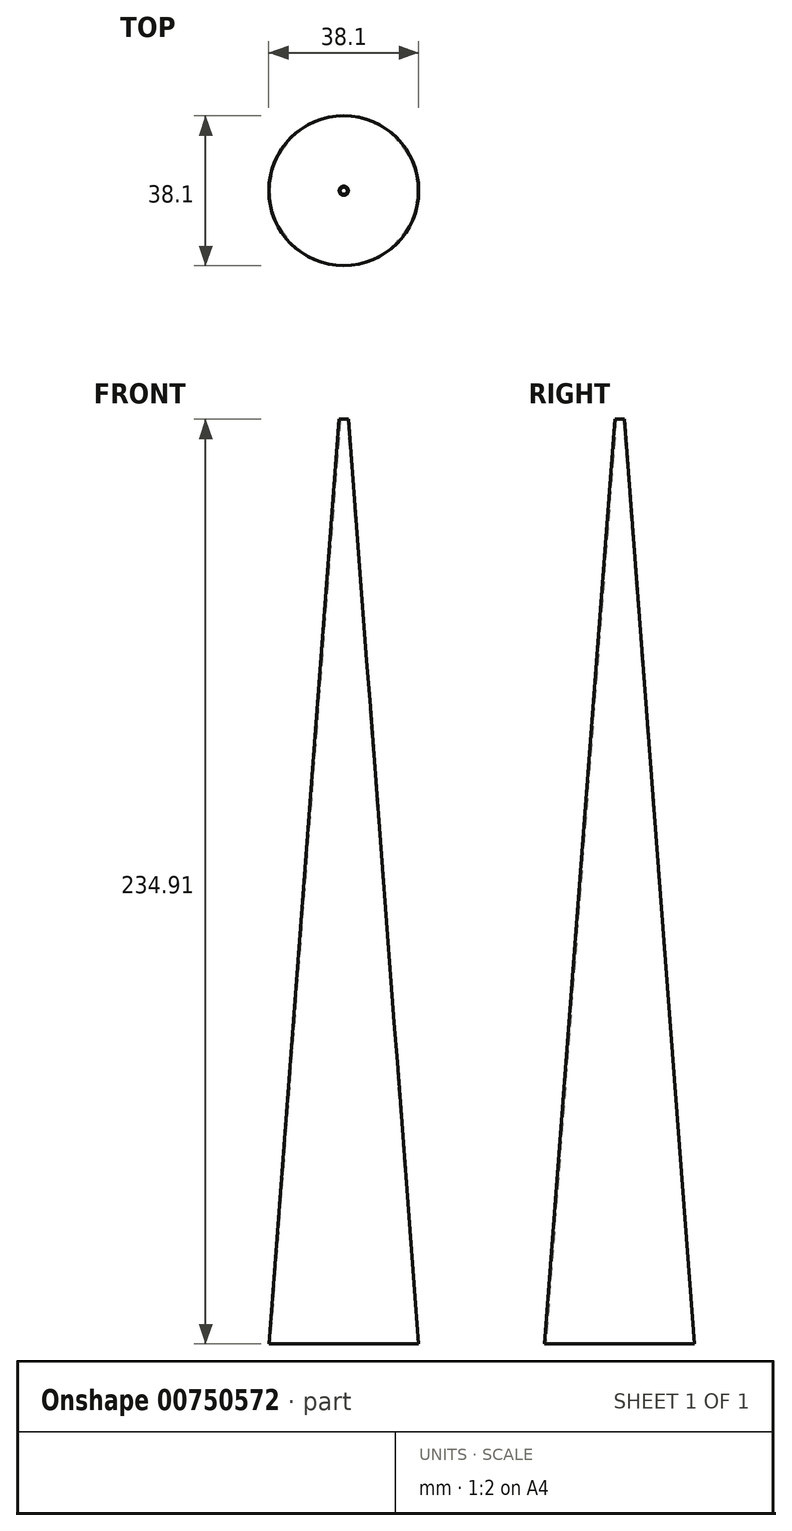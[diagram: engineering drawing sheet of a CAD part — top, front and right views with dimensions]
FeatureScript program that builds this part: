
annotation { "Feature Type Name" : "Feature", "Feature Type Description" : "" }
export const myFeature = defineFeature(function(context is Context, id is Id, definition is map)
    precondition{}
    {
        {
            var Q0;
            Q0=qCreatedBy(makeId("Front.planeOp"),FACE);
            var sketch = newSketch(context, id + "F0", { "sketchPlane" : qUnion([Q0])});
            skLineSegment(sketch, "E0", {"start": v(0, -52.04) * mm, "end": v(-19.05, -52.04) * mm});
            skLineSegment(sketch, "E1", {"start": v(0, 182.87) * mm, "end": v(-1.16, 182.87) * mm});
            skLineSegment(sketch, "E2", {"start": v(-1.16, 182.87) * mm, "end": v(-19.05, -52.04) * mm});
            skLineSegment(sketch, "E3", {"start": v(0, 182.87) * mm, "end": v(0, -52.04) * mm});
            skSolve(sketch);
        }
        {
            var Q0;
            Q0 = qSketchRegion(id + "F0", true);
            var Q1;
            Q1=sQuery(id+"F0.wireOp",EDGE,"E3");
            revolve(context, id + "F1", {"surfaceOperationType" : NewSurfaceOperationType.NEW, "entities" : qUnion([Q0]), "axis" : qUnion([Q1]), "revolveType" : RevolveType.FULL});
        }
        {
            var Q0;
            Q0=makeQuery(id+"F1.opRevolve","SWEPT_FACE",FACE,{"disambiguationData":[OSD([sQuery(id+"F0.wireOp",EDGE,"E0")])]});
            var Q1;
            Q1=makeQuery(id+"F1.opRevolve","SWEPT_FACE",FACE,{"disambiguationData":[OSD([sQuery(id+"F0.wireOp",EDGE,"E1")])]});
            shell(context, id + "F2", {"entities" : qUnion([Q0, Q1]), "thickness" : 0.25 * mm});
        }
    });
